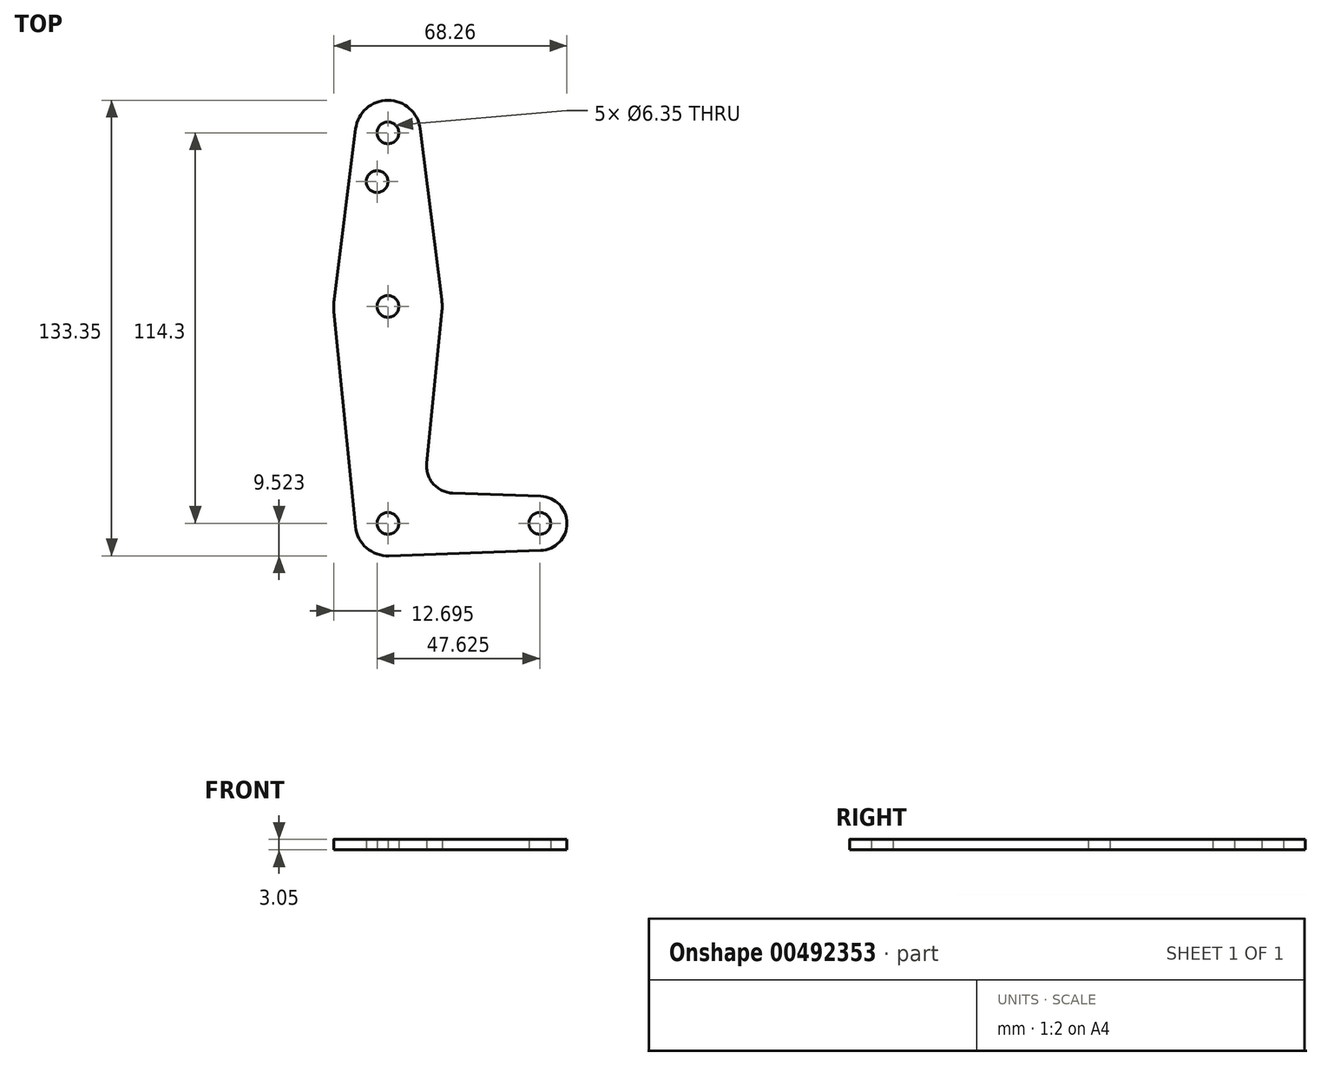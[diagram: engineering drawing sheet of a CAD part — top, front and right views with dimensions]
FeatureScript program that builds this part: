
annotation { "Feature Type Name" : "Feature", "Feature Type Description" : "" }
export const myFeature = defineFeature(function(context is Context, id is Id, definition is map)
    precondition{}
    {
        {
            var Q0;
            Q0=qCreatedBy(makeId("Top.planeOp"),FACE);
            var sketch = newSketch(context, id + "F0", { "sketchPlane" : qUnion([Q0])});
            skCircle(sketch, "E0", {"center": v(0, 58.04) * mm, "radius": 9.53 * mm});
            skCircle(sketch, "E1", {"center": v(0, 7.24) * mm, "radius": 15.88 * mm});
            skCircle(sketch, "E2", {"center": v(0, -56.26) * mm, "radius": 9.53 * mm});
            skCircle(sketch, "E3", {"center": v(44.45, -56.26) * mm, "radius": 7.94 * mm});
            skLineSegment(sketch, "E4", {"start": v(0, 58.04) * mm, "end": v(0, -56.26) * mm, "construction": true});
            skLineSegment(sketch, "E5", {"start": v(0, -56.26) * mm, "end": v(44.45, -56.26) * mm, "construction": true});
            skLineSegment(sketch, "E6", {"start": v(-9.45, 59.23) * mm, "end": v(-15.75, 9.23) * mm});
            skLineSegment(sketch, "E7", {"start": v(9.45, 59.23) * mm, "end": v(15.75, 9.23) * mm});
            skLineSegment(sketch, "E8", {"start": v(-9.48, -57.2) * mm, "end": v(-15.8, 5.66) * mm});
            skLineSegment(sketch, "E9", {"start": v(11.34, -38.66) * mm, "end": v(15.8, 5.66) * mm});
            skLineSegment(sketch, "E10", {"start": v(0.34, -65.78) * mm, "end": v(44.73, -64.19) * mm});
            skLineSegment(sketch, "E11", {"start": v(44.73, -48.32) * mm, "end": v(18.97, -47.4) * mm});
            skCircle(sketch, "E12", {"center": v(0, 58.04) * mm, "radius": 3.18 * mm});
            skCircle(sketch, "E13", {"center": v(0, 7.24) * mm, "radius": 3.18 * mm});
            skCircle(sketch, "E14", {"center": v(0, -56.26) * mm, "radius": 3.18 * mm});
            skCircle(sketch, "E15", {"center": v(44.45, -56.26) * mm, "radius": 3.18 * mm});
            skCircle(sketch, "E16", {"center": v(-3.17, 43.77) * mm, "radius": 3.18 * mm});
            skArc(sketch, "E17.filletArc", {"start": v(11.34, -38.66) * mm, "mid": v(13.26, -44.69) * mm, "end": v(18.97, -47.4) * mm});
            skSolve(sketch);
        }
        {
            var Q0;
            Q0 = qSketchRegion(id + "F0", true);
            extrude(context, id + "F1", {"entities" : qUnion([Q0]), "depth" : 3.05 * mm});
        }
    });
